# Revit family: Seating-Casual-Naughtone-Polly_SL
name_source: partatom
category: Furniture
revit_build: Autodesk Revit 2015 (Build: 20150704_0715(x64)
units: mm (PartAtom-declared; Revit-internal decimal feet)

## types (1)
- POLLY-CH-SL
    AdditionalMaterials = Additional material and finish options available. Please contact Naughtone direct for further information.
    Assembly Code = E2020
    AssetIdentifier = POLLY-CH-SL
    AssetType = Movable
    BIMObjectName = Seating-Casual-Naughtone-Polly_SL
    BarCode = 0.000000
    Category = 40.50.12 : Chairs, Seats and Benches
    CodePerformance = FISP Certified; ISO14001 Certified
    Color = White
    ComponentDescription = The Polly chair fundamentally provides a very comfortable ergonomic seat with as little visual detail as possible. The Polypropylene seat shell has subtle edge details, a soft texture and just the right amount of flex, all of which combine to provide a tactile and satisfying sitting experience.
    Constituents = Polypropylene; Steel frame
    Cost = 0 $
    Description = Polly Chair Sled Base
    DurationUnit = Years
    ExpectedLife = 15-20
    Finish = Polyster powder coat; various seat colour finishes available
    Keynote = 40.50.12
    Manufacturer = Naughtone
    ManufacturerAddressUK = 201 Pannal Business Park, Station Road, Harrogate, HG3 1JL
    Material = Glass re-enforced polypropylene; steel frame
    Model = POLLY-CH-SL
    ModelNumber = POLLY-CH-SL
    ModelReference = Polly Chair Sled Base
    NBSReference = 40.50.12
    Name = 524mmx530mmx785mm, Polly Chair Sled Base
    NominalHeight = 785 mm
    NominalLength = 530 mm  [stored 1.73885 ft]
    NominalWidth = 524 mm  [stored 1.71916 ft]
    Option = Sled Base
    Product URL = http://www.naughtone.com
    ProductInformation = http://www.naughtone.com
    ReplacementCost = 0.00
    SeatHeight = 450 mm  [stored 1.47638 ft]
    SerialNumber = 0.000000
    Shape = Organic
    Size = 524mmx530mmx785mm
    SustainabilityPerformance = 99% recyclable. 127% recycled & recyclable content
    TagNumber = 0.000000
    Type Comments = 524x530x785
    TypeName = Seating-Casual-Naughtone-Polly_SL
    URL = http://www.naughtone.com
    Uniclass2015 = 40.50.12
    Version = 1
    WarrantyDescription = 5 year warranty
    WarrantyDurationLabor = 5
    WarrantyDurationParts = 5
    WarrantyDurationUnit = Years
    _BIMspec_GUID = 0
    _current revision = 1
    _distributed by = www.bimbox.co.uk

note: [stored X ft] marks values corroborated as IEEE doubles in the binary element streams (Revit-internal decimal feet)

## geometry (parser evidence)
native form markers: Sweep x7
no freeform markers — native parametric forms only
